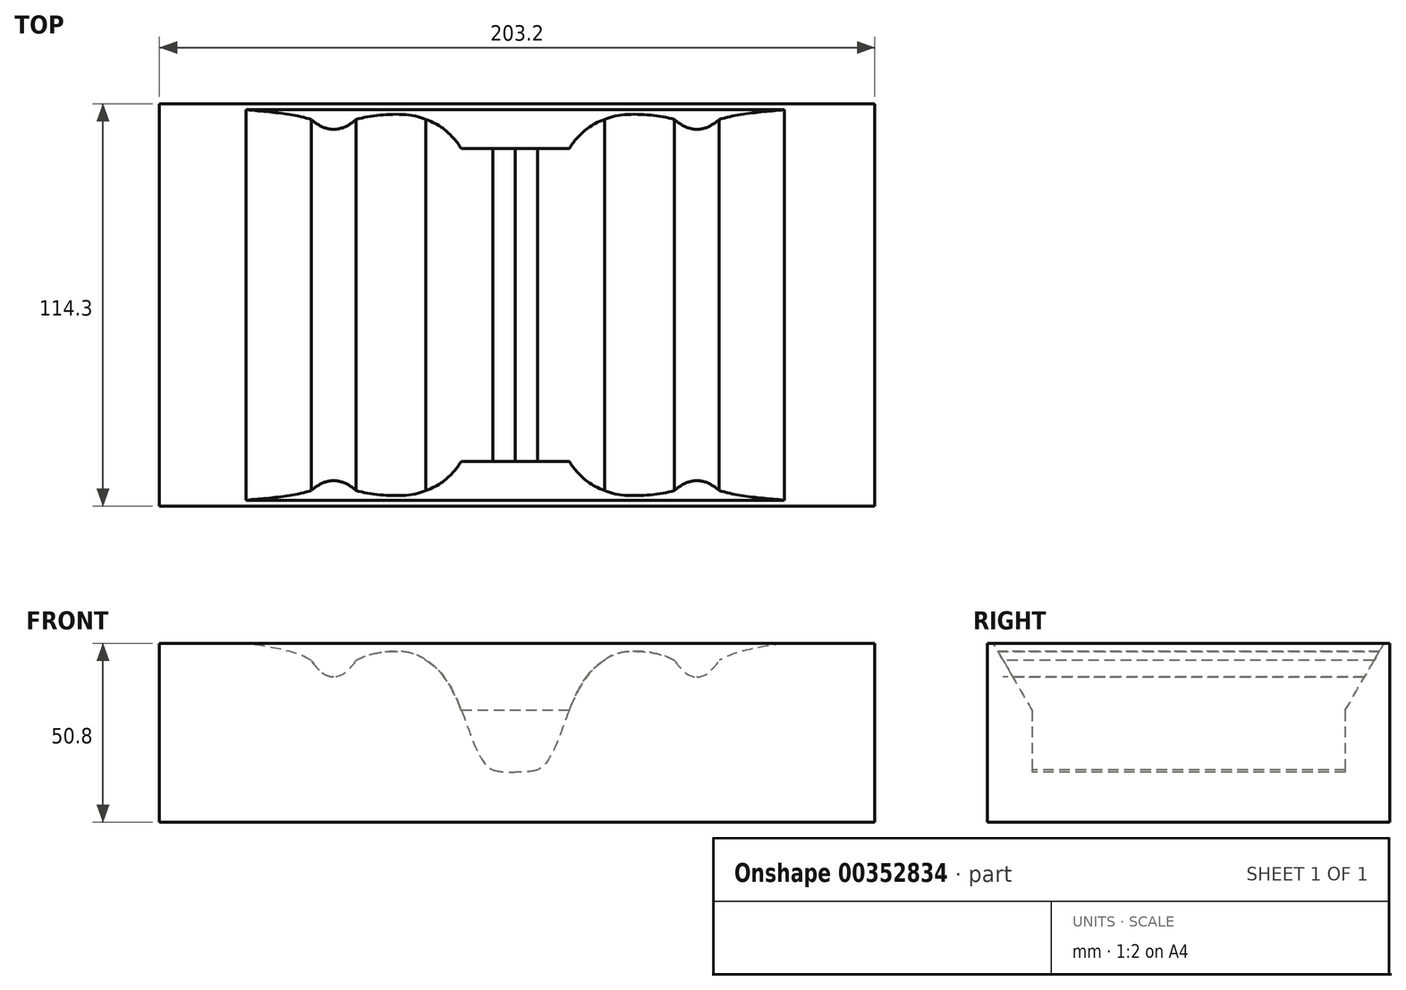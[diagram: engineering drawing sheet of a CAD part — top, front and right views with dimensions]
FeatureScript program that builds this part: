
annotation { "Feature Type Name" : "Feature", "Feature Type Description" : "" }
export const myFeature = defineFeature(function(context is Context, id is Id, definition is map)
    precondition{}
    {
        {
            var Q0;
            Q0=qCreatedBy(makeId("Front.planeOp"),FACE);
            var sketch = newSketch(context, id + "F0", { "sketchPlane" : qUnion([Q0])});
            skLineSegment(sketch, "E0.bottom", {"start": v(0, 0) * mm, "end": v(203.2, 0) * mm});
            skLineSegment(sketch, "E0.top", {"start": v(0, 50.8) * mm, "end": v(203.2, 50.8) * mm});
            skLineSegment(sketch, "E0.left", {"start": v(0, 0) * mm, "end": v(0, 50.8) * mm});
            skLineSegment(sketch, "E0.right", {"start": v(203.2, 0) * mm, "end": v(203.2, 50.8) * mm});
            skSolve(sketch);
        }
        {
            var Q0;
            Q0 = qSketchRegion(id + "F0", true);
            extrude(context, id + "F1", {"entities" : qUnion([Q0]), "oppositeDirection" : true, "depth" : 114.3 * mm});
        }
        {
            var Q0;
            Q0=makeQuery(id+"F1.opExtrude","CAP_FACE",FACE,{"disambiguationData":[OSD([sQuery(id+"F0.wireOp",EDGE,"E0.bottom"),sQuery(id+"F0.wireOp",EDGE,"E0.top"),sQuery(id+"F0.wireOp",EDGE,"E0.left"),sQuery(id+"F0.wireOp",EDGE,"E0.right")])],"isStart":true});
            var sketch = newSketch(context, id + "F2", { "sketchPlane" : qUnion([Q0])});
            skPoint(sketch, "E1", {"position": v(101.07, 62.26) * mm});
            skLineSegment(sketch, "E2", {"start": v(101.07, 58.7) * mm, "end": v(101.07, 33.3) * mm});
            skFitSpline(sketch, "E3", {"points": [v(202.14, 58.67) * mm, v(202.14, 64.2) * mm, v(199.65, 65.9) * mm, v(194.25, 64.77) * mm, v(101.07, 58.7) * mm], "startDerivative": vector(7.76, 43.3) * mm, "endDerivative": vector(-205.13, -9.01) * mm});
            skFitSpline(sketch, "E4.MirrorCS", {"points": [v(0, 58.67) * mm, v(0, 64.2) * mm, v(2.5, 65.9) * mm, v(7.9, 64.77) * mm, v(101.07, 58.7) * mm], "startDerivative": vector(-7.76, 43.3) * mm, "endDerivative": vector(205.13, -9.01) * mm});
            skPoint(sketch, "E5", {"position": v(-2.2, 29.44) * mm});
            skPoint(sketch, "E6", {"position": v(-2.2, -2.31) * mm});
            skPoint(sketch, "E7", {"position": v(-53.79, 2.45) * mm});
            skPoint(sketch, "E8", {"position": v(-60.14, -2.31) * mm});
            skPoint(sketch, "E9", {"position": v(-47.44, -2.31) * mm});
            skFitSpline(sketch, "E10", {"points": [v(202.14, 58.67) * mm, v(186.05, 52.06) * mm, v(159.02, 46) * mm, v(152.67, 41.23) * mm, v(146.32, 46) * mm, v(126.47, 46) * mm], "startDerivative": vector(-29.98, -50.18) * mm, "endDerivative": vector(-51.07, -50.34) * mm});
            skPoint(sketch, "E11", {"position": v(-27.6, -2.31) * mm});
            skPoint(sketch, "E12", {"position": v(31.9, 67.75) * mm});
            skFitSpline(sketch, "E13", {"points": [v(159.02, 46) * mm, v(152.67, 41.23) * mm, v(146.32, 46) * mm], "startDerivative": vector(-12.7, -19.05) * mm, "endDerivative": vector(-12.7, 19.05) * mm});
            skPoint(sketch, "E14", {"position": v(-8.54, 28.8) * mm});
            skFitSpline(sketch, "E15", {"points": [v(126.47, 46) * mm, v(107.42, 14.88) * mm], "startDerivative": vector(-33.81, -18.92) * mm, "endDerivative": vector(-21.6, -9.65) * mm});
            skFitSpline(sketch, "E16", {"points": [v(107.42, 14.88) * mm, v(101.07, 14.24) * mm], "startDerivative": vector(-6.53, -2.04) * mm, "endDerivative": vector(-5.8, -0.15) * mm});
            skFitSpline(sketch, "E17.MirrorCS", {"points": [v(75.67, 46) * mm, v(94.72, 14.88) * mm], "startDerivative": vector(33.81, -18.92) * mm, "endDerivative": vector(21.6, -9.65) * mm});
            skFitSpline(sketch, "E18.MirrorCS", {"points": [v(94.72, 14.88) * mm, v(101.07, 14.24) * mm], "startDerivative": vector(6.53, -2.04) * mm, "endDerivative": vector(5.8, -0.15) * mm});
            skFitSpline(sketch, "E19.MirrorCS", {"points": [v(0, 58.67) * mm, v(16.1, 52.06) * mm, v(43.13, 46) * mm, v(49.48, 41.23) * mm, v(55.83, 46) * mm, v(75.67, 46) * mm], "startDerivative": vector(29.98, -50.18) * mm, "endDerivative": vector(51.07, -50.34) * mm});
            skFitSpline(sketch, "E20.MirrorCS", {"points": [v(43.13, 46) * mm, v(49.48, 41.23) * mm, v(55.83, 46) * mm], "startDerivative": vector(12.7, -19.05) * mm, "endDerivative": vector(12.7, 19.05) * mm});
            skSolve(sketch);
        }
        {
            var Q0;
            Q0 = qSketchRegion(id + "F2", true);
            extrude(context, id + "F3", {"entities" : qUnion([Q0]), "operationType" : NewBodyOperationType.REMOVE, "oppositeDirection" : true, "depth" : 101.6 * mm, "hasSecondDirection" : true, "secondDirectionOppositeDirection" : true, "secondDirectionDepth" : 12.7 * mm});
        }
        {
            var Q0;
            Q0=makeQuery(id+"F3.boolean.opBoolean","INTERSECT",EDGE,{"derivedFrom":[makeQuery(id+"F1.opExtrude","SWEPT_FACE",FACE,{"disambiguationData":[OSD([sQuery(id+"F0.wireOp",EDGE,"E0.top")])]}),makeQuery(id+"F3.opExtrude","CAP_FACE",FACE,{"disambiguationData":[OSD([sQuery(id+"F2.wireOp",EDGE,"E3"),sQuery(id+"F2.wireOp",EDGE,"E4.MirrorCS"),sQuery(id+"F2.wireOp",EDGE,"E10"),sQuery(id+"F2.wireOp",EDGE,"E10"),sQuery(id+"F2.wireOp",EDGE,"E13"),sQuery(id+"F2.wireOp",EDGE,"E15"),sQuery(id+"F2.wireOp",EDGE,"E16"),sQuery(id+"F2.wireOp",EDGE,"E17.MirrorCS"),sQuery(id+"F2.wireOp",EDGE,"E18.MirrorCS"),sQuery(id+"F2.wireOp",EDGE,"E19.MirrorCS"),sQuery(id+"F2.wireOp",EDGE,"E20.MirrorCS"),sQuery(id+"F2.wireOp",EDGE,"E19.MirrorCS")])],"isStart":false})]});
            var Q1;
            Q1=makeQuery(id+"F3.boolean.opBoolean","INTERSECT",EDGE,{"derivedFrom":[makeQuery(id+"F1.opExtrude","SWEPT_FACE",FACE,{"disambiguationData":[OSD([sQuery(id+"F0.wireOp",EDGE,"E0.top")])]}),makeQuery(id+"F3.opExtrude","CAP_FACE",FACE,{"disambiguationData":[OSD([sQuery(id+"F2.wireOp",EDGE,"E3"),sQuery(id+"F2.wireOp",EDGE,"E4.MirrorCS"),sQuery(id+"F2.wireOp",EDGE,"E10"),sQuery(id+"F2.wireOp",EDGE,"E10"),sQuery(id+"F2.wireOp",EDGE,"E13"),sQuery(id+"F2.wireOp",EDGE,"E15"),sQuery(id+"F2.wireOp",EDGE,"E16"),sQuery(id+"F2.wireOp",EDGE,"E17.MirrorCS"),sQuery(id+"F2.wireOp",EDGE,"E18.MirrorCS"),sQuery(id+"F2.wireOp",EDGE,"E19.MirrorCS"),sQuery(id+"F2.wireOp",EDGE,"E20.MirrorCS"),sQuery(id+"F2.wireOp",EDGE,"E19.MirrorCS")])],"isStart":true})]});
            chamfer(context, id + "F4", {"entities" : qUnion([Q0, Q1]), "chamferType" : ChamferType.OFFSET_ANGLE, "width" : 19.05 * mm, "oppositeDirection" : false, "angle" : 30 * degree, "tangentPropagation" : true});
        }
    });
